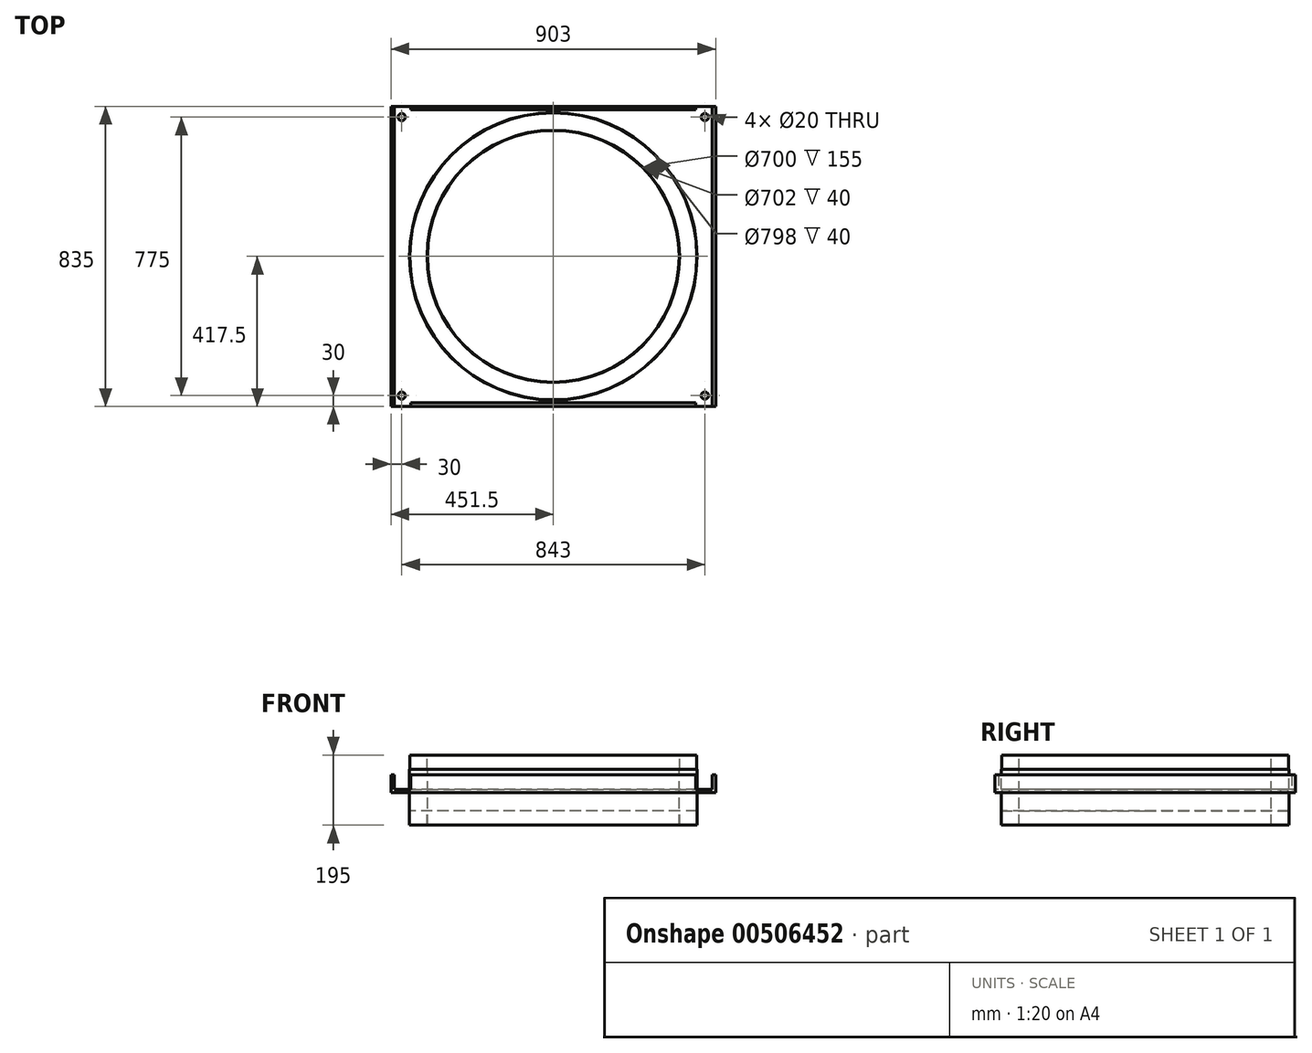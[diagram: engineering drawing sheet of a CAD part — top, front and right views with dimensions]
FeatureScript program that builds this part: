
annotation { "Feature Type Name" : "Feature", "Feature Type Description" : "" }
export const myFeature = defineFeature(function(context is Context, id is Id, definition is map)
    precondition{}
    {
        {
            var Q0;
            Q0=qCreatedBy(makeId("Front.planeOp"),FACE);
            var sketch = newSketch(context, id + "F0", { "sketchPlane" : qUnion([Q0])});
            skLineSegment(sketch, "E0", {"start": v(0, 74.87) * mm, "end": v(0, -73.71) * mm, "construction": true});
            skLineSegment(sketch, "E1", {"start": v(0, 374.84) * mm, "end": v(0, -528.94) * mm, "construction": true});
            skLineSegment(sketch, "E2", {"start": v(-350, -100) * mm, "end": v(-350, 55) * mm});
            skLineSegment(sketch, "E3", {"start": v(-350, 55) * mm, "end": v(-351, 55) * mm});
            skLineSegment(sketch, "E4", {"start": v(-351, 55) * mm, "end": v(-351, 95) * mm});
            skLineSegment(sketch, "E5", {"start": v(-351, 95) * mm, "end": v(-399, 95) * mm});
            skLineSegment(sketch, "E6", {"start": v(-399, 95) * mm, "end": v(-399, 55) * mm});
            skLineSegment(sketch, "E7", {"start": v(-399, 55) * mm, "end": v(-400, 55) * mm});
            skLineSegment(sketch, "E8", {"start": v(-400, 55) * mm, "end": v(-400, -100) * mm});
            skLineSegment(sketch, "E9", {"start": v(-400, -100) * mm, "end": v(-399, -100) * mm});
            skLineSegment(sketch, "E10", {"start": v(-399, -100) * mm, "end": v(-399, -60) * mm});
            skLineSegment(sketch, "E11", {"start": v(-399, -60) * mm, "end": v(-351, -60) * mm});
            skLineSegment(sketch, "E12", {"start": v(-351, -60) * mm, "end": v(-351, -100) * mm});
            skLineSegment(sketch, "E13", {"start": v(-351, -100) * mm, "end": v(-350, -100) * mm});
            skSolve(sketch);
        }
        {
            var Q0;
            Q0=qSketchRegion(id+"F0",true);
            var Q1;
            Q1=sQuery(id+"F0.wireOp",EDGE,"E1");
            revolve(context, id + "F1", {"entities" : qUnion([Q0]), "axis" : qUnion([Q1]), "revolveType" : RevolveType.FULL});
        }
        {
            var Q0;
            Q0=qCreatedBy(makeId("Top.planeOp"),FACE);
            var sketch = newSketch(context, id + "F2", { "sketchPlane" : qUnion([Q0])});
            skLineSegment(sketch, "E14.bottom", {"start": v(451.5, 417.5) * mm, "end": v(-451.5, 417.5) * mm});
            skLineSegment(sketch, "E14.top", {"start": v(451.5, -417.5) * mm, "end": v(-451.5, -417.5) * mm});
            skLineSegment(sketch, "E14.left", {"start": v(451.5, 417.5) * mm, "end": v(451.5, -417.5) * mm});
            skLineSegment(sketch, "E14.right", {"start": v(-451.5, 417.5) * mm, "end": v(-451.5, -417.5) * mm});
            skPoint(sketch, "E14.middle", {"position": v(0, 0) * mm});
            skCircle(sketch, "E15.0", {"center": v(0, 0) * mm, "radius": 351 * mm});
            skCircle(sketch, "E16.0", {"center": v(0, 0) * mm, "radius": 350 * mm});
            skCircle(sketch, "E17", {"center": v(0, 0) * mm, "radius": 400 * mm});
            skLineSegment(sketch, "E18", {"start": v(0, 0) * mm, "end": v(0, 773.78) * mm, "construction": true});
            skLineSegment(sketch, "E19", {"start": v(0, 0) * mm, "end": v(1007.48, 0) * mm, "construction": true});
            skCircle(sketch, "E20", {"center": v(421.5, 387.5) * mm, "radius": 10 * mm});
            skCircle(sketch, "E21.MirrorC", {"center": v(-421.5, 387.5) * mm, "radius": 10 * mm});
            skCircle(sketch, "E22.MirrorC", {"center": v(421.5, -387.5) * mm, "radius": 10 * mm});
            skCircle(sketch, "E23.MirrorC", {"center": v(-421.5, -387.5) * mm, "radius": 10 * mm});
            skSolve(sketch);
        }
        {
            var Q0;
            Q0=qSketchRegion(id+"F2",true);
            extrude(context, id + "F3", {"entities" : qUnion([Q0]), "operationType" : NewBodyOperationType.ADD, "oppositeDirection" : true, "depth" : 10 * mm});
        }
        {
            var Q0;
            Q0=makeQuery(id+"F3.opExtrude","CAP_FACE",FACE,{"disambiguationData":[OSD([sQuery(id+"F2.wireOp",EDGE,"E14.bottom"),sQuery(id+"F2.wireOp",EDGE,"E14.top"),sQuery(id+"F2.wireOp",EDGE,"E14.left"),sQuery(id+"F2.wireOp",EDGE,"E14.right"),sQuery(id+"F2.wireOp",EDGE,"E17"),sQuery(id+"F2.wireOp",EDGE,"E20"),sQuery(id+"F2.wireOp",EDGE,"E21.MirrorC"),sQuery(id+"F2.wireOp",EDGE,"E22.MirrorC"),sQuery(id+"F2.wireOp",EDGE,"E23.MirrorC")])],"isStart":false});
            var sketch = newSketch(context, id + "F4", { "sketchPlane" : qUnion([Q0])});
            skLineSegment(sketch, "E24", {"start": v(0, 0) * mm, "end": v(-1098.02, 0) * mm, "construction": true});
            skLineSegment(sketch, "E25", {"start": v(0, 0) * mm, "end": v(0, -1084.2) * mm, "construction": true});
            skLineSegment(sketch, "E26.bottom", {"start": v(396.5, 417.5) * mm, "end": v(-396.5, 417.5) * mm});
            skLineSegment(sketch, "E26.top", {"start": v(396.5, 407.5) * mm, "end": v(-396.5, 407.5) * mm});
            skLineSegment(sketch, "E26.left", {"start": v(396.5, 417.5) * mm, "end": v(396.5, 407.5) * mm});
            skLineSegment(sketch, "E26.right", {"start": v(-396.5, 417.5) * mm, "end": v(-396.5, 407.5) * mm});
            skLineSegment(sketch, "E27.bottom", {"start": v(-451.5, 417.5) * mm, "end": v(-441.5, 417.5) * mm});
            skLineSegment(sketch, "E27.top", {"start": v(-451.5, -417.5) * mm, "end": v(-441.5, -417.5) * mm});
            skLineSegment(sketch, "E27.left", {"start": v(-451.5, 417.5) * mm, "end": v(-451.5, -417.5) * mm});
            skLineSegment(sketch, "E27.right", {"start": v(-441.5, 417.5) * mm, "end": v(-441.5, -417.5) * mm});
            skLineSegment(sketch, "E28.MirrorCS", {"start": v(396.5, -417.5) * mm, "end": v(396.5, -407.5) * mm});
            skLineSegment(sketch, "E29.MirrorCS", {"start": v(-396.5, -417.5) * mm, "end": v(-396.5, -407.5) * mm});
            skLineSegment(sketch, "E30.MirrorCS", {"start": v(396.5, -407.5) * mm, "end": v(-396.5, -407.5) * mm});
            skLineSegment(sketch, "E31.MirrorCS", {"start": v(396.5, -417.5) * mm, "end": v(-396.5, -417.5) * mm});
            skLineSegment(sketch, "E32.MirrorCS", {"start": v(451.5, -417.5) * mm, "end": v(441.5, -417.5) * mm});
            skLineSegment(sketch, "E33.MirrorCS", {"start": v(451.5, 417.5) * mm, "end": v(441.5, 417.5) * mm});
            skLineSegment(sketch, "E34.MirrorCS", {"start": v(451.5, 417.5) * mm, "end": v(451.5, -417.5) * mm});
            skLineSegment(sketch, "E35.MirrorCS", {"start": v(441.5, 417.5) * mm, "end": v(441.5, -417.5) * mm});
            skLineSegment(sketch, "E36.MirrorCS", {"start": v(0, 0) * mm, "end": v(1098.02, 0) * mm, "construction": true});
            skSolve(sketch);
        }
        {
            var Q0;
            Q0=qSketchRegion(id+"F4",true);
            extrude(context, id + "F5", {"entities" : qUnion([Q0]), "operationType" : NewBodyOperationType.ADD, "oppositeDirection" : true, "depth" : 50 * mm});
        }
    });
